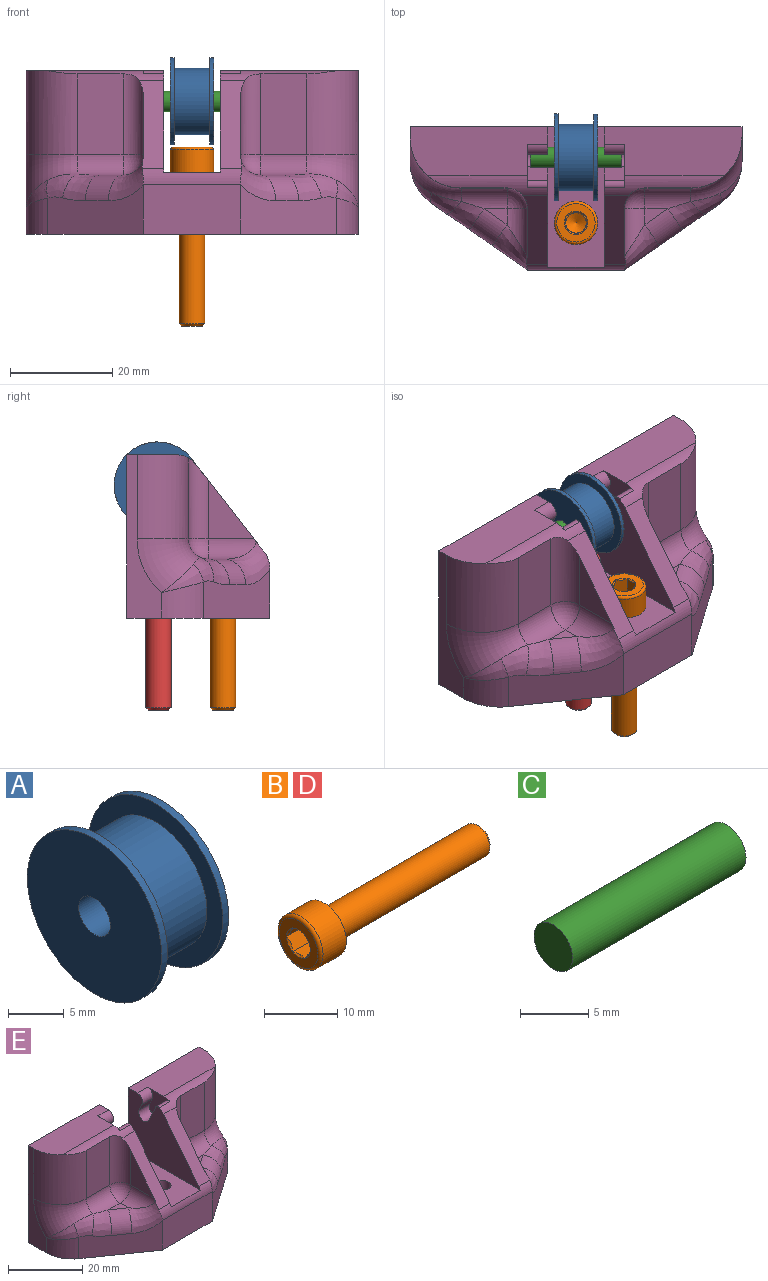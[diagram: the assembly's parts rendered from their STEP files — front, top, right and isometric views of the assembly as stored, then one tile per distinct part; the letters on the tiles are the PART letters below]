
ASSEMBLY  parts=5 mates=4
PART A: 8 faces, bbox 8.5x17x17 mm
  f0: cylinder r=6.5mm len=13mm, axis (-1,0,0), area 285.9mm2, adj f3,f6
  f1: cylinder r=8.5mm len=17mm, axis (-1,0,0), area 40.1mm2, adj f2,f3
  f2: plane 17x17mm, normal (1,0,0), area 214.4mm2, adj f1,f7
  f3: plane 17x17mm, normal (-1,0,0), area 94.2mm2, adj f0,f1
  f4: cylinder r=8.5mm len=17mm, axis (1,0,0), area 40.1mm2, adj f5,f6
  f5: plane 17x17mm, normal (-1,0,0), area 214.4mm2, adj f4,f7
  f6: plane 17x17mm, normal (1,0,0), area 94.2mm2, adj f0,f4
  f7: cylinder r=2mm len=8.5mm, axis (1,0,0), area 106.8mm2, adj f2,f5
PART B: 29 faces, bbox 35x9.2x9.2 mm
  f0: cone r=2mm half-angle=45deg, axis (-1,0,0), area 0.6mm2, adj f6,f22
  f1: cone r=2mm half-angle=45deg, axis (-1,0,0), area 0.6mm2, adj f6,f23
  f2: cone r=2mm half-angle=45deg, axis (-1,0,0), area 0.6mm2, adj f6,f24
  f3: cone r=2mm half-angle=45deg, axis (-1,0,0), area 0.6mm2, adj f6,f26
  f4: cone r=2mm half-angle=45deg, axis (-1,0,0), area 0.6mm2, adj f6,f25
  f5: cone r=2mm half-angle=45deg, axis (-1,0,0), area 0.6mm2, adj f6,f27
  f6: plane 7.5x7.5mm, normal (-1,0,0), area 27.7mm2, adj f0,f1,f2,f3,f4,f5,f7,f22
  f7: torus R=3.75mm, axis (1,0,0), area 20.1mm2, adj f6,f8
  f8: cylinder r=4.25mm len=8.5mm, axis (1,0,0), area 120.2mm2, adj f7,f9
  f9: plane 8.5x8.5mm, normal (1,0,0), area 31.2mm2, adj f8,f10
  f10: torus R=2.85mm, axis (1,0,0), area 4.2mm2, adj f9,f11
  f11: cone r=2.66mm half-angle=20.6deg, axis (-1,0,0), area 6.9mm2, adj f10,f12
  f12: torus R=2.7mm, axis (1,0,0), area 1.1mm2, adj f11,f13
  f13: cylinder r=2.5mm len=28.91mm, axis (1,0,0), area 454.1mm2, adj f12,f14
  f14: cone r=2.5mm half-angle=45deg, axis (-1,0,0), area 9.8mm2, adj f13,f15
  f15: plane 4.02x4.02mm, normal (1,0,0), area 12.7mm2, adj f14
  f16: plane 1.73x1mm, normal (-1,0,0), area 0.2mm2, adj f24,f25,f28
  f17: plane 2x0.58mm, normal (-1,0,0), area 0.2mm2, adj f23,f24,f28
  f18: plane 1.73x1mm, normal (-1,0,0), area 0.2mm2, adj f22,f23,f28
  f19: plane 1.73x1mm, normal (-1,0,0), area 0.2mm2, adj f22,f27,f28
  f20: plane 2x0.58mm, normal (-1,0,0), area 0.2mm2, adj f26,f27,f28
  f21: plane 1.73x1mm, normal (-1,0,0), area 0.2mm2, adj f25,f26,f28
  f22: plane 3.1x2.31mm, normal (0,0,-1), area 6.7mm2, adj f0,f6,f18,f19,f23,f27
  f23: plane 3.1x2mm, normal (0,0.87,-0.5), area 6.7mm2, adj f1,f6,f17,f18,f22,f24
  f24: plane 3.1x2mm, normal (0,0.87,0.5), area 6.7mm2, adj f2,f6,f16,f17,f23,f25
  f25: plane 3.1x2.31mm, normal (0,0,1), area 6.7mm2, adj f4,f6,f16,f21,f24,f26
  f26: plane 3.1x2mm, normal (0,-0.87,0.5), area 6.7mm2, adj f3,f6,f20,f21,f25,f27
  f27: plane 3.1x2mm, normal (0,-0.87,-0.5), area 6.7mm2, adj f5,f6,f19,f20,f22,f26
  f28: cone r=0mm half-angle=60deg, axis (-1,0,0), area 14.5mm2, adj f16,f17,f18,f19,f20,f21
PART C: 3 faces, bbox 18x4x4 mm
  f0: cylinder r=2mm len=18mm, axis (-1,0,0), area 226.2mm2, adj f1,f2
  f1: plane 4x4mm, normal (1,0,0), area 12.6mm2, adj f0
  f2: plane 4x4mm, normal (-1,0,0), area 12.6mm2, adj f0
PART D: same geometry as B
PART E: 67 faces, bbox 65.2x29.6x32.2 mm
  f0: cylinder r=2mm len=4mm, axis (-1,0,0), area 25.1mm2, adj f14,f21,f57,f58
  f1: cylinder r=2mm len=4mm, axis (-1,0,0), area 25.1mm2, adj f2,f19,f55,f56
  f2: plane 27.49x20mm, normal (-1,0,0), area 360.1mm2, adj f1,f7,f8,f11,f15,f43,f55,f56
  f3: plane 17.4x13.63mm, normal (0,-0.79,0.62), area 88.9mm2, adj f13,f14,f31,f33,f41,f43,f63
  f4: plane 15.84x9mm, normal (0,-1,0), area 142.6mm2, adj f30,f31,f45,f63
  f5: plane 15.84x9mm, normal (0,-1,0), area 142.6mm2, adj f35,f37,f50,f64
  f6: plane 27x9.56mm, normal (0,0,1), area 225.7mm2, adj f11,f14,f20,f21,f45,f59,f63
  f7: plane 27x9.56mm, normal (0,0,1), area 225.7mm2, adj f2,f11,f18,f19,f50,f61,f64
  f8: plane 17.4x13.63mm, normal (0,-0.79,0.62), area 88.9mm2, adj f2,f12,f34,f35,f43,f44,f64
  f9: plane 19x9.8mm, normal (0,-1,0), area 186.2mm2, adj f10,f27,f29,f41,f43,f44
  f10: plane 65x28mm, normal (0,0,-1), area 1414.8mm2, adj f9,f11,f16,f17,f18,f20,f27,f29
  f11: plane 65x32mm, normal (0,1,0), area 1754.4mm2, adj f2,f6,f7,f10,f14,f15,f18,f20
  f12: plane 11.36x8.88mm, normal (1,0,0), area 50.4mm2, adj f8,f34,f35
  f13: plane 11.36x8.88mm, normal (-1,0,0), area 50.4mm2, adj f3,f31,f33
  f14: plane 27.49x20mm, normal (1,0,0), area 360.1mm2, adj f0,f3,f6,f11,f15,f43,f57,f58
  f15: plane 27.49x11mm, normal (0,0,1), area 273.3mm2, adj f2,f11,f14,f16,f17,f43
  f16: cylinder r=2.15mm len=12mm, axis (0,0,1), area 162.2mm2, adj f10,f15
  f17: cylinder r=2.15mm len=12mm, axis (0,0,1), area 162.2mm2, adj f10,f15
  f18: plane 32x6.78mm, normal (1,0,0), area 103.2mm2, adj f7,f10,f11,f50,f51,f52
  f19: plane 8.46x8mm, normal (-1,0,0), area 35.2mm2, adj f1,f7,f55,f56,f61,f62,f64,f65
  f20: plane 32x6.78mm, normal (-1,0,0), area 103.2mm2, adj f6,f10,f11,f45,f46,f49
  f21: plane 8.46x8mm, normal (1,0,0), area 35.2mm2, adj f0,f6,f57,f58,f59,f60,f63,f66
  f22: cylinder r=4.1mm len=10mm, axis (0,1,0), area 257.6mm2, adj f11,f23
  f23: plane 8.2x8.2mm, normal (0,1,0), area 52.8mm2, adj f22
  f24: cylinder r=4.1mm len=10mm, axis (0,1,0), area 257.6mm2, adj f11,f25
  f25: plane 8.2x8.2mm, normal (0,1,0), area 52.8mm2, adj f24
  f26: plane 4.49x3.13mm, normal (0,0,1), area 7mm2, adj f34,f37,f42
  f27: plane 18.71x13.02mm, normal (0.57,-0.82,0), area 160.2mm2, adj f9,f10,f40,f42,f44,f51,f54
  f28: plane 4.49x3.13mm, normal (0,0,1), area 7mm2, adj f30,f33,f39
  f29: plane 18.71x13.02mm, normal (-0.57,-0.82,0), area 160.2mm2, adj f9,f10,f38,f39,f41,f47,f49
  f30: cylinder r=4mm len=9mm, axis (-1,0,0), area 53.3mm2, adj f4,f28,f32,f38,f46
  f31: cylinder r=4mm len=15.84mm, axis (0,0,-1), area 89.5mm2, adj f3,f4,f13,f32,f63
  f32: sphere r=4mm, area 23.7mm2, adj f30,f31,f33
  f33: cylinder r=4mm len=9.32mm, axis (0,-1,0), area 44.5mm2, adj f3,f13,f28,f32,f41
  f34: cylinder r=4mm len=9.32mm, axis (0,1,0), area 44.5mm2, adj f8,f12,f26,f36,f44
  f35: cylinder r=4mm len=15.84mm, axis (0,0,-1), area 89.5mm2, adj f5,f8,f12,f36,f64
  f36: sphere r=4mm, area 25.1mm2, adj f34,f35,f37
  f37: cylinder r=4mm len=9mm, axis (-1,0,0), area 53.3mm2, adj f5,f26,f36,f40,f52
  f38: bspline ~7.36x5.5mm, area 35mm2, adj f29,f30,f39,f47
  f39: cylinder r=5mm len=7.35mm, axis (-0.82,0.57,0), area 43mm2, adj f28,f29,f38,f41
  f40: bspline ~7.36x5.5mm, area 35mm2, adj f27,f37,f42,f54
  f41: bspline ~10.3x8.91mm, area 54.6mm2, adj f3,f9,f29,f33,f39,f43
  f42: cylinder r=5mm len=7.35mm, axis (-0.82,-0.57,0), area 43mm2, adj f26,f27,f40,f44
  f43: cylinder r=5mm len=19.43mm, axis (-1,0,0), area 52.4mm2, adj f2,f3,f8,f9,f14,f15,f41,f44
  f44: bspline ~10.3x8.91mm, area 54.6mm2, adj f8,f9,f27,f34,f42,f43
  f45: cylinder r=10mm len=16.48mm, axis (0,0,-1), area 256.6mm2, adj f4,f6,f20,f46,f63
  f46: torus R=14mm, axis (-1,0,0), area 116.4mm2, adj f20,f30,f45,f47,f48
  f47: bspline ~9.16x6.07mm, area 24.3mm2, adj f29,f38,f46,f48
  f48: bspline ~8.5x5.8mm, area 13.8mm2, adj f46,f47,f49
  f49: cylinder r=10mm len=8.21mm, axis (0,0,-1), area 58mm2, adj f10,f20,f29,f48
  f50: cylinder r=10mm len=16.48mm, axis (0,0,1), area 256.6mm2, adj f5,f7,f18,f52,f64
  f51: cylinder r=10mm len=8.21mm, axis (0,0,1), area 58mm2, adj f10,f18,f27,f53
  f52: torus R=14mm, axis (1,0,0), area 116.4mm2, adj f18,f37,f50,f53,f54
  f53: bspline ~8.5x5.8mm, area 13.8mm2, adj f51,f52,f54
  f54: bspline ~7.68x5.28mm, area 24.3mm2, adj f27,f40,f52,f53
  f55: plane 4x2.3mm, normal (0,-0.91,-0.43), area 10.2mm2, adj f1,f2,f19,f61
  f56: plane 5.72x4mm, normal (0,0.91,0.43), area 25.3mm2, adj f1,f2,f19,f62
  f57: plane 4x2.3mm, normal (0,-0.91,-0.43), area 10.2mm2, adj f0,f14,f21,f59
  f58: plane 5.72x4mm, normal (0,0.91,0.43), area 25.3mm2, adj f0,f14,f21,f60
  f59: cylinder r=2mm len=4mm, axis (1,0,0), area 16.1mm2, adj f6,f14,f21,f57
  f60: cylinder r=2mm len=4mm, axis (1,0,0), area 0.7mm2, adj f14,f21,f58,f66
  f61: cylinder r=2mm len=4mm, axis (1,0,0), area 16.1mm2, adj f2,f7,f19,f55
  f62: cylinder r=2mm len=4mm, axis (1,0,0), area 0.7mm2, adj f2,f19,f56,f65
  f63: cylinder r=5mm len=23.54mm, axis (-1,0,0), area 54.6mm2, adj f3,f4,f6,f14,f21,f31,f45,f66
  f64: cylinder r=5mm len=23.54mm, axis (-1,0,0), area 54.6mm2, adj f2,f5,f7,f8,f19,f35,f50,f65
  f65: cylinder r=1mm len=4mm, axis (1,0,0), area 6.1mm2, adj f2,f19,f62,f64
  f66: cylinder r=1mm len=4mm, axis (1,0,0), area 6.1mm2, adj f14,f21,f60,f63
PLACE A rot(axis=(-1,0,0),160.1deg) t=(-0.02,7.59,7.59)mm
PLACE B rot(axis=(0,1,0),90deg) t=(-0.02,-5.21,-6.41)mm
PLACE C rot(axis=(1,0,0),19.9deg) t=(-0.02,36.57,12.66)mm
PLACE D rot(axis=(0,1,0),90deg) t=(-0.02,7.41,-6.41)mm
PLACE E t=(-0.02,-0.41,-2.41)mm fixed
MATE revolute C.f0 <-> A.f0  axis (-1,0,0) through (-0.02,7.59,7.59)mm
MATE revolute D.f0 <-> E.f17  axis (0,0,-1) through (-0.02,7.41,-6.41)mm
MATE revolute A.f0 <-> E.f0  axis (1,0,0) through (-0.02,7.59,7.59)mm
MATE revolute B.f0 <-> E.f16  axis (0,0,-1) through (-0.02,-5.21,-6.41)mm
